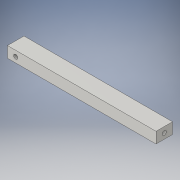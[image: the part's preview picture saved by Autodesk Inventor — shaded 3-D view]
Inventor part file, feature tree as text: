
AUTODESK INVENTOR PART (.ipt)
format: ipt  version: 2016 (Build 200138000, 138)  size: 118,272 bytes
history: native  units: in
note: dims shown in document units (in); Inventor stores cm internally (conversion verified against a paired STEP export)
features: extrude x3, sketch x3
ambient origin geometry x8: Origin, YZ Plane, XZ Plane, XY Plane, X Axis, Y Axis, Z Axis, Center Point
bodies: Solid1 (feature_tree)
feature tree (6):
  extrude  "Extrusion1"  Depth=0.75in
  extrude  "Extrusion2"  Depth=0.5in
  extrude  "Extrusion3"  Depth=0.5in
  sketch  "Sketch1"  dims[d0=6.75in d1=0.75in]
  sketch  "Sketch2"  dims[d2=0.5in d3=0.0in d4=0.1875in]
  sketch  "Sketch3"  dims[d5=0.5in d6=0.0in d7=0.375in d8=0.1875in d9=0.5in d10=0.0in]
